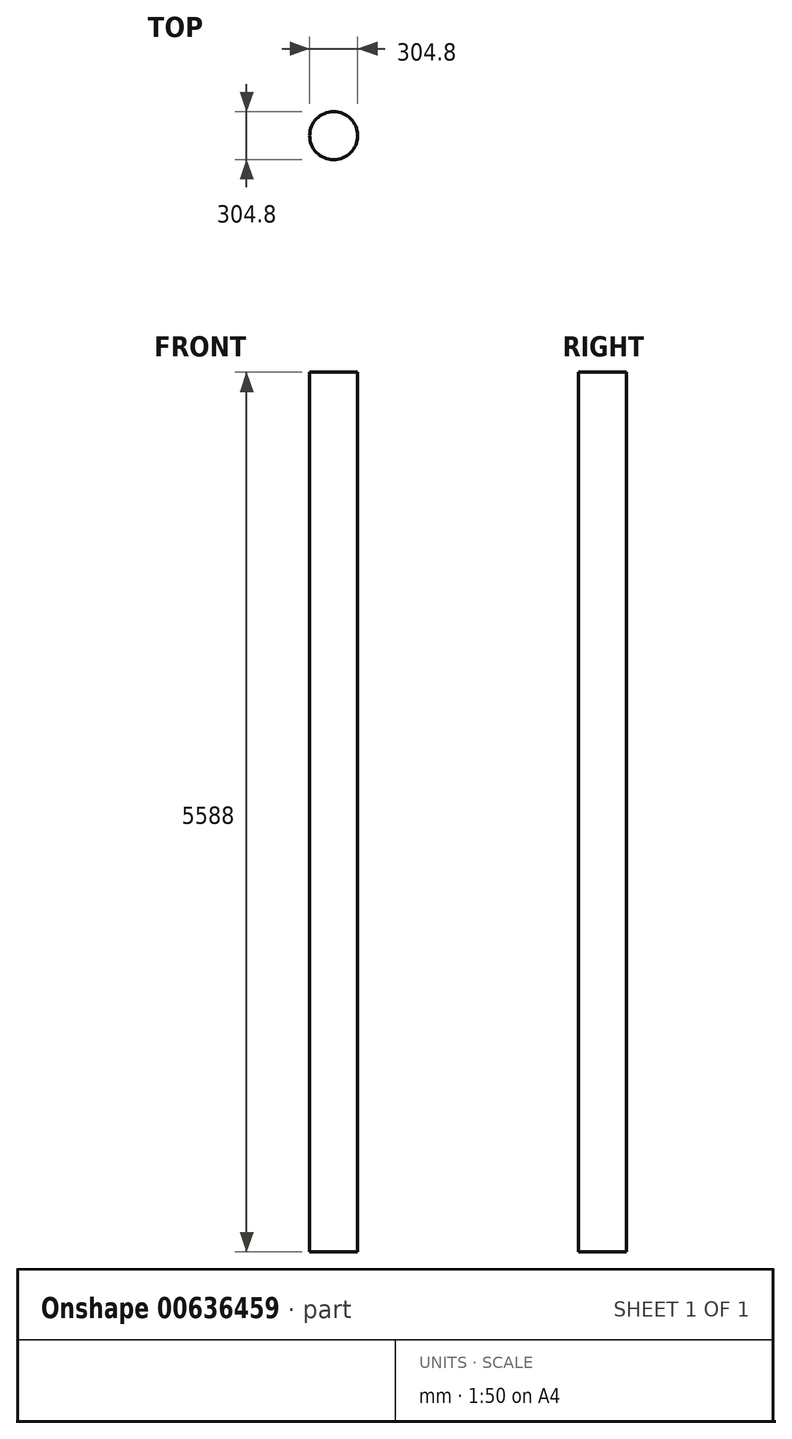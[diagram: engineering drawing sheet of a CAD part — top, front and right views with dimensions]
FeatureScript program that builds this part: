
annotation { "Feature Type Name" : "Feature", "Feature Type Description" : "" }
export const myFeature = defineFeature(function(context is Context, id is Id, definition is map)
    precondition{}
    {
        {
            var Q0;
            Q0=qCreatedBy(makeId("Top.planeOp"),FACE);
            var sketch = newSketch(context, id + "F0", { "sketchPlane" : qUnion([Q0])});
            skCircle(sketch, "E0", {"center": v(0, 0) * mm, "radius": 152.4 * mm});
            skSolve(sketch);
        }
        {
            var Q0;
            Q0 = qSketchRegion(id + "F0", true);
            extrude(context, id + "F1", {"entities" : qUnion([Q0]), "depth" : 5588 * mm, "offsetDistance" : 25.4 * mm});
        }
    });
